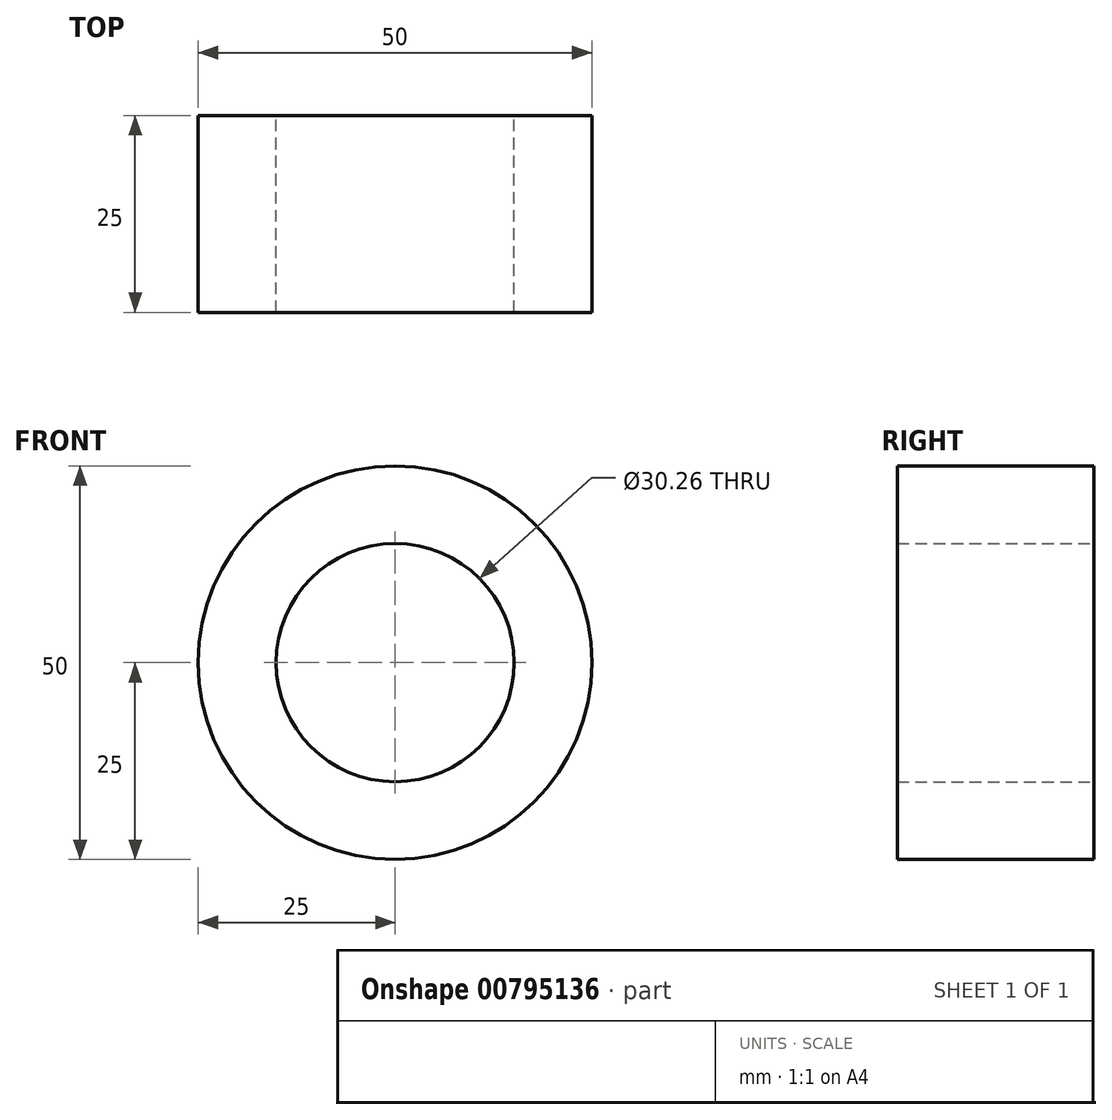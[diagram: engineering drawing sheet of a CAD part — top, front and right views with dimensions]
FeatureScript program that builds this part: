
annotation { "Feature Type Name" : "Feature", "Feature Type Description" : "" }
export const myFeature = defineFeature(function(context is Context, id is Id, definition is map)
    precondition{}
    {
        {
            var Q0;
            Q0=qCreatedBy(makeId("Front.planeOp"),FACE);
            var sketch = newSketch(context, id + "F0", { "sketchPlane" : qUnion([Q0])});
            skCircle(sketch, "E0", {"center": v(0, 0) * mm, "radius": 25 * mm});
            skCircle(sketch, "E1", {"center": v(0, 0) * mm, "radius": 15.13 * mm});
            skCircle(sketch, "E2", {"center": v(90, 0) * mm, "radius": 15 * mm});
            skSolve(sketch);
        }
        {
            var Q0;
            {var subQ0=sQuery(id+"F0.wireOp",EDGE,"7a334c51-4027-4b71-b380-c4215b3a4bb8");var subQ1=sQuery(id+"F0.wireOp",EDGE,"E0");var subQ2=makeQuery(id+"F0.imprint","INTERSECT",VERTEX,{"disambiguationData":[OD(0.0)],"derivedFrom":[subQ1,subQ0]});Q0=makeQuery(id+"F0.imprint","IMPRINT",FACE,{"disambiguationData":[TD([[makeQuery(id+"F0.imprint","IMPRINT",EDGE,{"disambiguationData":[TD([[subQ2,-1.0]])],"derivedFrom":subQ1}),1.0]])]});}
            var Q1;
            {var subQ0=sQuery(id+"F0.wireOp",EDGE,"acc67311-bd1d-4d11-b9e1-fbc97a02bc88");Q1=makeQuery(id+"F0.imprint","IMPRINT",FACE,{"disambiguationData":[TD([[makeQuery(id+"F0.imprint","IMPRINT",EDGE,{"derivedFrom":subQ0}),1.0]])]});}
            var Q2;
            Q2=makeQuery(id+"F0.imprint","IMPRINT",FACE,{"disambiguationData":[TD([[makeQuery(id+"F0.imprint","IMPRINT",EDGE,{"derivedFrom":sQuery(id+"F0.wireOp",EDGE,"0d817a87-66d6-4400-93f2-954fc7c4aac1")}),1.0]])]});
            extrude(context, id + "F1", {"entities" : qUnion([Q0, Q1, Q2]), "depth" : 25 * mm, "offsetDistance" : 25 * mm});
        }
    });
